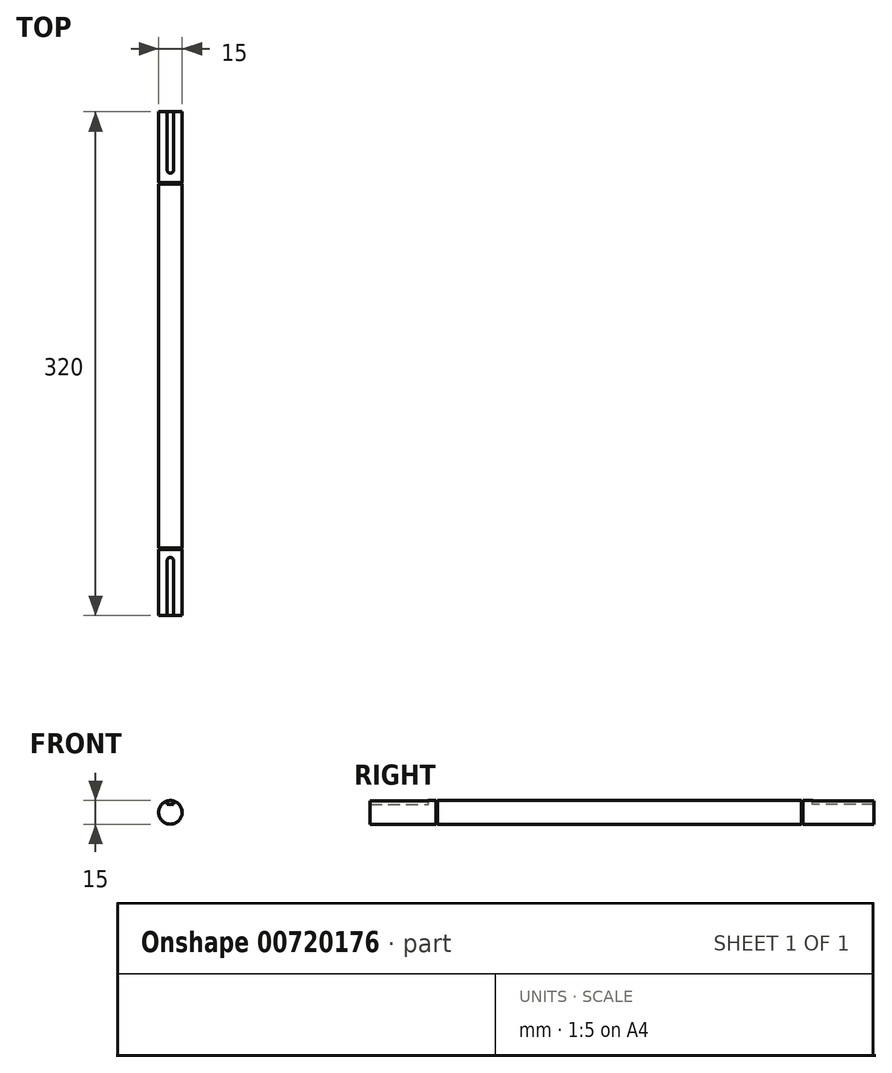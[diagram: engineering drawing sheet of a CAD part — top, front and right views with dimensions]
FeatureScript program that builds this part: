
annotation { "Feature Type Name" : "Feature", "Feature Type Description" : "" }
export const myFeature = defineFeature(function(context is Context, id is Id, definition is map)
    precondition{}
    {
        {
            var Q0;
            Q0=qCreatedBy(makeId("Front.planeOp"),FACE);
            var sketch = newSketch(context, id + "F0", { "sketchPlane" : qUnion([Q0])});
            skCircle(sketch, "E0", {"center": v(0, 0) * mm, "radius": 7.5 * mm});
            skSolve(sketch);
        }
        {
            var Q0;
            Q0=makeQuery(id+"F0.imprint","IMPRINT",FACE,{"disambiguationData":[TD([[makeQuery(id+"F0.imprint","IMPRINT",EDGE,{"derivedFrom":sQuery(id+"F0.wireOp",EDGE,"E0")}),1.0]])]});
            extrude(context, id + "F1", {"entities" : qUnion([Q0]), "depth" : 320 * mm, "offsetDistance" : 25 * mm});
        }
        {
            var Q0;
            Q0=qCreatedBy(makeId("Top.planeOp"),FACE);
            cPlane(context, id + "F2", {"entities" : qUnion([Q0]), "cplaneType" : CPlaneType.OFFSET, "offset" : 7.5 * mm, "width" : 150 * mm, "height" : 150 * mm});
        }
        {
            var Q0;
            Q0=qCreatedBy(id+"F2.planeOp",FACE);
            var sketch = newSketch(context, id + "F3", { "sketchPlane" : qUnion([Q0])});
            skLineSegment(sketch, "E1.bottom", {"start": v(-2, 0) * mm, "end": v(2, 0) * mm});
            skLineSegment(sketch, "E1.top", {"start": v(0, -39) * mm, "end": v(0, -39) * mm});
            skLineSegment(sketch, "E1.left", {"start": v(-2, 0) * mm, "end": v(-2, -37) * mm});
            skLineSegment(sketch, "E1.right", {"start": v(2, 0) * mm, "end": v(2, -37) * mm});
            skPoint(sketch, "E2.visualSharp", {"position": v(2, -39) * mm});
            skArc(sketch, "E2.filletArc", {"start": v(0, -39) * mm, "mid": v(1.41, -38.41) * mm, "end": v(2, -37) * mm});
            skPoint(sketch, "E3.visualSharp", {"position": v(-2, -39) * mm});
            skArc(sketch, "E3.filletArc", {"start": v(-2, -37) * mm, "mid": v(-1.41, -38.41) * mm, "end": v(0, -39) * mm});
            skLineSegment(sketch, "E4.bottom", {"start": v(2, -320) * mm, "end": v(-2, -320) * mm});
            skLineSegment(sketch, "E4.top", {"start": v(0, -283) * mm, "end": v(0, -283) * mm});
            skLineSegment(sketch, "E4.left", {"start": v(2, -320) * mm, "end": v(2, -285) * mm});
            skLineSegment(sketch, "E4.right", {"start": v(-2, -320) * mm, "end": v(-2, -285) * mm});
            skPoint(sketch, "E5.visualSharp", {"position": v(-2, -283) * mm});
            skArc(sketch, "E5.filletArc", {"start": v(0, -283) * mm, "mid": v(-1.41, -283.59) * mm, "end": v(-2, -285) * mm});
            skPoint(sketch, "E6.visualSharp", {"position": v(2, -283) * mm});
            skArc(sketch, "E6.filletArc", {"start": v(2, -285) * mm, "mid": v(1.41, -283.59) * mm, "end": v(0, -283) * mm});
            skSolve(sketch);
        }
        {
            var Q0;
            Q0 = qSketchRegion(id + "F3", true);
            extrude(context, id + "F4", {"entities" : qUnion([Q0]), "operationType" : NewBodyOperationType.REMOVE, "oppositeDirection" : true, "depth" : 2.5 * mm, "offsetDistance" : 25 * mm});
        }
        {
            var Q0;
            Q0=makeQuery(id+"F1.opExtrude","CAP_FACE",FACE,{"disambiguationData":[OSD([sQuery(id+"F0.wireOp",EDGE,"E0")])],"isStart":false});
            cPlane(context, id + "F5", {"entities" : qUnion([Q0]), "cplaneType" : CPlaneType.OFFSET, "offset" : 42 * mm, "oppositeDirection" : true, "width" : 150 * mm, "height" : 150 * mm});
        }
        {
            var Q0;
            Q0=qCreatedBy(id+"F5.planeOp",FACE);
            var sketch = newSketch(context, id + "F6", { "sketchPlane" : qUnion([Q0])});
            skCircle(sketch, "E7", {"center": v(0, 0) * mm, "radius": 7 * mm});
            skCircle(sketch, "E8", {"center": v(0, 0) * mm, "radius": 7.5 * mm});
            skSolve(sketch);
        }
        {
            var Q0;
            Q0 = qSketchRegion(id + "F6", true);
            extrude(context, id + "F7", {"entities" : qUnion([Q0]), "operationType" : NewBodyOperationType.REMOVE, "oppositeDirection" : true, "depth" : 1 * mm, "offsetDistance" : 25 * mm});
        }
        {
            var Q0;
            Q0=makeQuery(id+"F1.opExtrude","CAP_FACE",FACE,{"disambiguationData":[OSD([sQuery(id+"F0.wireOp",EDGE,"E0")])],"isStart":true});
            cPlane(context, id + "F8", {"entities" : qUnion([Q0]), "cplaneType" : CPlaneType.OFFSET, "offset" : 45 * mm, "oppositeDirection" : true, "width" : 150 * mm, "height" : 150 * mm});
        }
        {
            var Q0;
            Q0=qCreatedBy(id+"F8.planeOp",FACE);
            var sketch = newSketch(context, id + "F9", { "sketchPlane" : qUnion([Q0])});
            skCircle(sketch, "E9", {"center": v(0, 0) * mm, "radius": 7 * mm});
            skCircle(sketch, "E10", {"center": v(0, 0) * mm, "radius": 7.5 * mm});
            skSolve(sketch);
        }
        {
            var Q0;
            Q0 = qSketchRegion(id + "F9", true);
            extrude(context, id + "F10", {"entities" : qUnion([Q0]), "operationType" : NewBodyOperationType.REMOVE, "oppositeDirection" : true, "depth" : 1 * mm, "offsetDistance" : 25 * mm});
        }
    });
